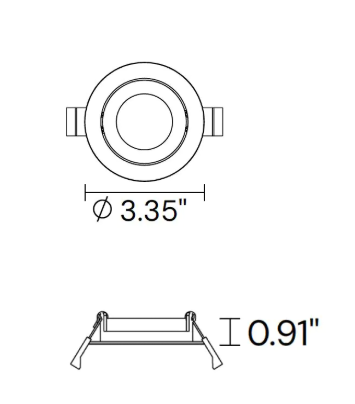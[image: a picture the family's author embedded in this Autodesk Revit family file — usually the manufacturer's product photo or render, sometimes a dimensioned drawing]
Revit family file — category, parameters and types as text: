
# Revit family: Alcon-14078-4 -Revit-Family
name_source: partatom
category: Lighting Fixtures
units: mm (PartAtom-declared; Revit-internal decimal feet)

## family parameters
Always vertical = Yes
Cut with Voids When Loaded = No
Host = Ceiling
Light Source = Yes
OmniClass Number = 23.80.70.11
OmniClass Title = Luminaries for Internal Lighting
Part Type = Normal
Room Calculation Point = No
Round Connector Dimension = Use Diameter
Shared = No

## types (1)
- Type 1
    Color Filter = 16777215
    Default Elevation = 0' - 0"
    Dimming Lamp Color Temperature Shift = <None>
    Housing = Default
    Light Source Symbol Length = 10' - 0"
    LightSource = light
    Link To Product Page = https://www.alconlighting.com
    Manufacturer = Alcon Light
    Product Identity = Alcon Lighting 14078-4
    Reflector = Default metal
    Spot Beam Angle = 30.00°
    Spot Field Angle = 90.00°
    Tilt Angle = 60.00°

## geometry (parser evidence)
native form markers: Sweep x2
no freeform markers — native parametric forms only
